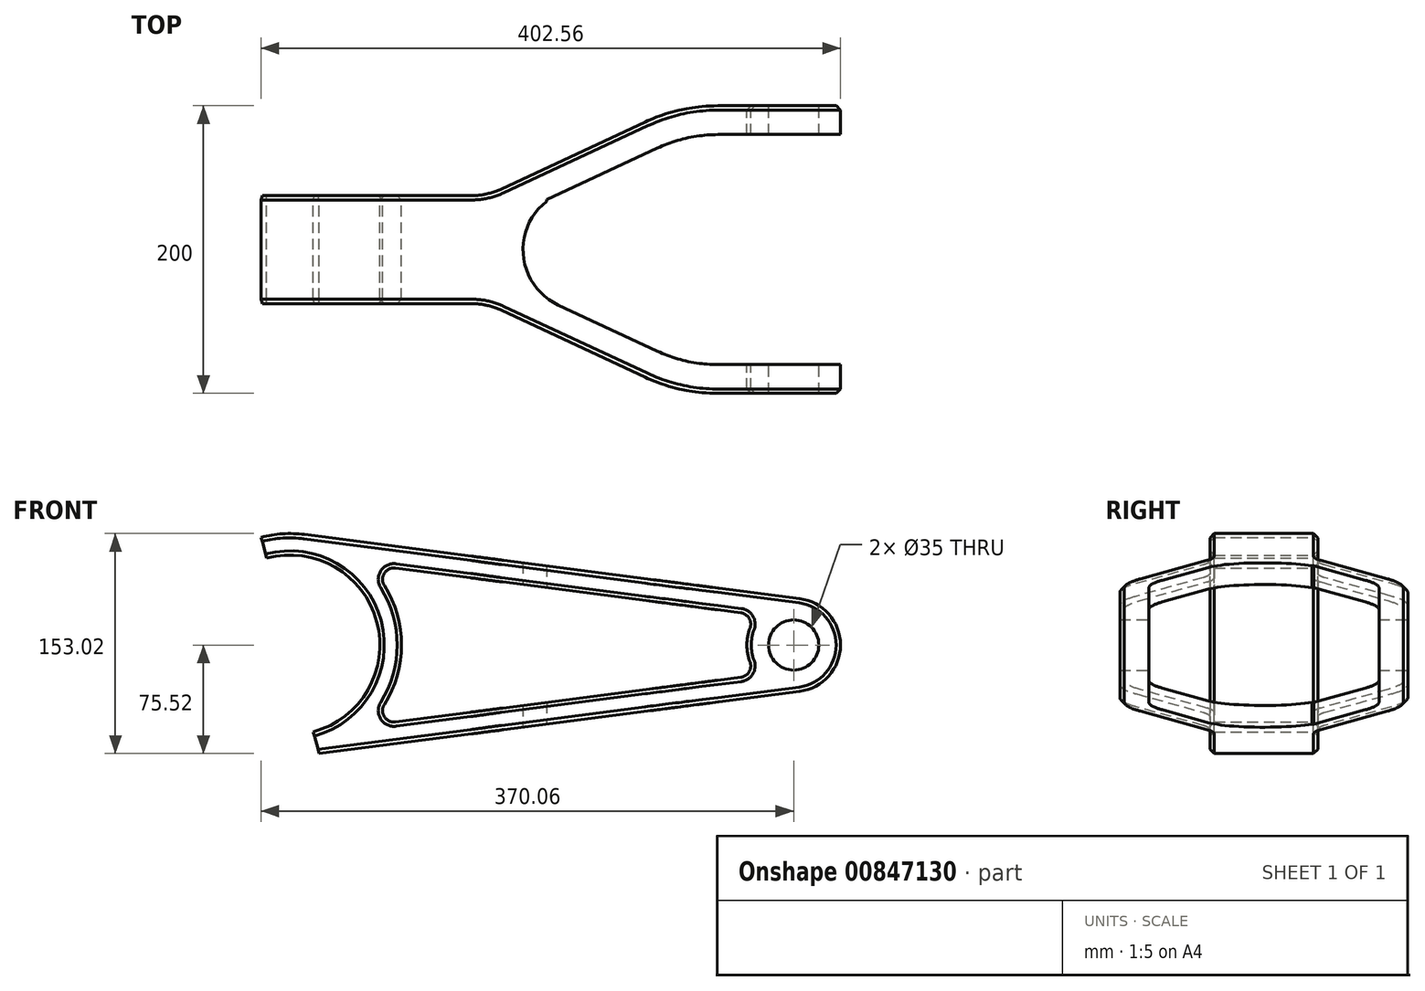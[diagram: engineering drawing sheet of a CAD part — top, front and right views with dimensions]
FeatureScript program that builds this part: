
annotation { "Feature Type Name" : "Feature", "Feature Type Description" : "" }
export const myFeature = defineFeature(function(context is Context, id is Id, definition is map)
    precondition{}
    {
        {
            var Q0;
            Q0=qCreatedBy(makeId("Top.planeOp"),FACE);
            var sketch = newSketch(context, id + "F0", { "sketchPlane" : qUnion([Q0])});
            skLineSegment(sketch, "E0", {"start": v(-175, 0) * mm, "end": v(53.2, 0) * mm, "construction": true});
            skLineSegment(sketch, "E1.bottom", {"start": v(207.5, 100) * mm, "end": v(122.5, 100) * mm});
            skLineSegment(sketch, "E1.top", {"start": v(207.5, -100) * mm, "end": v(-175, -100) * mm});
            skLineSegment(sketch, "E1.left", {"start": v(175, 100) * mm, "end": v(175, -100) * mm});
            skLineSegment(sketch, "E1.right", {"start": v(-175, 100) * mm, "end": v(-175, -100) * mm});
            skPoint(sketch, "E1.middle", {"position": v(0, 0) * mm});
            skLineSegment(sketch, "E2.0", {"start": v(207.5, 80) * mm, "end": v(122.5, 80) * mm});
            skLineSegment(sketch, "E3.0", {"start": v(122.5, 100) * mm, "end": v(122.5, -100) * mm, "construction": true});
            skLineSegment(sketch, "E4", {"start": v(80.24, 70.63) * mm, "end": v(11.37, 38.52) * mm});
            skArc(sketch, "E5", {"start": v(-13.17, 0) * mm, "mid": v(65.18, -22.84) * mm, "end": v(11.37, 38.52) * mm, "construction": true});
            skArc(sketch, "E6", {"start": v(11.37, 38.52) * mm, "mid": v(-6.51, 22.84) * mm, "end": v(-13.17, 0) * mm});
            skArc(sketch, "E7", {"start": v(80.24, 70.63) * mm, "mid": v(43.99, 41.93) * mm, "end": v(24.52, 0) * mm, "construction": true});
            skArc(sketch, "E8", {"start": v(24.52, 0) * mm, "mid": v(120.49, -119.98) * mm, "end": v(221.2, -3.96) * mm, "construction": true});
            skArc(sketch, "E9", {"start": v(122.5, 80) * mm, "mid": v(100.86, 77.63) * mm, "end": v(80.24, 70.63) * mm});
            skLineSegment(sketch, "E10", {"start": v(122.5, 80) * mm, "end": v(-175, 80) * mm});
            skArc(sketch, "E11", {"start": v(221.2, -3.96) * mm, "mid": v(187.3, 56.17) * mm, "end": v(122.5, 80) * mm, "construction": true});
            skLineSegment(sketch, "E12", {"start": v(11.37, 38.52) * mm, "end": v(-71.23, 0) * mm});
            skArc(sketch, "E13", {"start": v(122.5, 100) * mm, "mid": v(96.53, 97.16) * mm, "end": v(71.79, 88.76) * mm});
            skLineSegment(sketch, "E14.0", {"start": v(71.79, 88.76) * mm, "end": v(-118.55, 0) * mm});
            skPoint(sketch, "E15.orphan", {"position": v(-42.97, 0) * mm});
            skLineSegment(sketch, "E16", {"start": v(-175, 37.5) * mm, "end": v(-38.14, 37.5) * mm});
            skLineSegment(sketch, "E17.MirrorCS", {"start": v(-175, -37.5) * mm, "end": v(-38.14, -37.5) * mm});
            skLineSegment(sketch, "E18.MirrorCS", {"start": v(71.79, -88.76) * mm, "end": v(-118.55, 0) * mm});
            skLineSegment(sketch, "E19.MirrorCS", {"start": v(80.24, -70.63) * mm, "end": v(11.37, -38.52) * mm});
            skArc(sketch, "E20.MirrorCS", {"start": v(122.5, -80) * mm, "mid": v(100.86, -77.63) * mm, "end": v(80.24, -70.63) * mm});
            skLineSegment(sketch, "E21.MirrorCS", {"start": v(207.5, -80) * mm, "end": v(122.5, -80) * mm});
            skArc(sketch, "E22.MirrorCS", {"start": v(11.37, -38.52) * mm, "mid": v(-6.51, -22.84) * mm, "end": v(-13.17, 0) * mm});
            skLineSegment(sketch, "E23.0", {"start": v(207.5, 100) * mm, "end": v(207.5, -100) * mm});
            skPoint(sketch, "E24.orphan", {"position": v(175, 80) * mm});
            skPoint(sketch, "E25.orphan", {"position": v(175, -80) * mm});
            skArc(sketch, "E26", {"start": v(122.5, -100) * mm, "mid": v(96.53, -97.16) * mm, "end": v(71.79, -88.76) * mm});
            skArc(sketch, "E27", {"start": v(20.12, -42.6) * mm, "mid": v(19.73, -41.95) * mm, "end": v(19.34, -41.3) * mm});
            skLineSegment(sketch, "E28", {"start": v(122.5, 100) * mm, "end": v(-175, 100) * mm});
            skArc(sketch, "E29.trimOffspring", {"start": v(3.27, 33.57) * mm, "mid": v(3.34, 34.19) * mm, "end": v(3.42, 34.8) * mm});
            skArc(sketch, "E30.trimOffspring", {"start": v(20.12, 42.6) * mm, "mid": v(19.73, 41.95) * mm, "end": v(19.34, 41.3) * mm});
            skLineSegment(sketch, "E31.0", {"start": v(-205, 100) * mm, "end": v(-205, -100) * mm});
            skLineSegment(sketch, "E32", {"start": v(-175, -100) * mm, "end": v(-205, -100) * mm});
            skLineSegment(sketch, "E33", {"start": v(-175, 100) * mm, "end": v(-205, 100) * mm});
            skLineSegment(sketch, "E34", {"start": v(-175, 37.5) * mm, "end": v(-205, 37.5) * mm});
            skLineSegment(sketch, "E35", {"start": v(-175, -37.5) * mm, "end": v(-205, -37.5) * mm});
            skSolve(sketch);
        }
        {
            var Q0;
            {var subQ0=sQuery(id+"F0.wireOp",EDGE,"E34");Q0=makeQuery(id+"F0.imprint","IMPRINT",FACE,{"disambiguationData":[TD([[makeQuery(id+"F0.imprint","IMPRINT",EDGE,{"derivedFrom":subQ0}),1.0]])]});}
            var Q1;
            {var subQ1=sQuery(id+"F0.wireOp",EDGE,"E16");Q1=makeQuery(id+"F0.imprint","IMPRINT",FACE,{"disambiguationData":[TD([[makeQuery(id+"F0.imprint","IMPRINT",EDGE,{"derivedFrom":subQ1}),-1.0]])]});}
            var Q2;
            {var subQ9=sQuery(id+"F0.wireOp",EDGE,"E9");Q2=makeQuery(id+"F0.imprint","IMPRINT",FACE,{"disambiguationData":[TD([[makeQuery(id+"F0.imprint","IMPRINT",EDGE,{"derivedFrom":subQ9}),-1.0]])]});}
            var Q3;
            {var subQ9=sQuery(id+"F0.wireOp",EDGE,"E13");Q3=makeQuery(id+"F0.imprint","IMPRINT",FACE,{"disambiguationData":[TD([[makeQuery(id+"F0.imprint","IMPRINT",EDGE,{"derivedFrom":subQ9}),1.0]])]});}
            var Q4;
            {var subQ0=sQuery(id+"F0.wireOp",EDGE,"E23.0");var subQ1=sQuery(id+"F0.wireOp",EDGE,"E1.bottom");var subQ2=makeQuery(id+"F0.imprint","INTERSECT",VERTEX,{"derivedFrom":[subQ1,subQ0]});Q4=makeQuery(id+"F0.imprint","IMPRINT",FACE,{"disambiguationData":[TD([[makeQuery(id+"F0.imprint","IMPRINT",EDGE,{"disambiguationData":[TD([[subQ2,-1.0]])],"derivedFrom":subQ1}),1.0]])]});}
            var Q5;
            {var subQ0=sQuery(id+"F0.wireOp",EDGE,"E23.0");var subQ1=sQuery(id+"F0.wireOp",EDGE,"E1.top");var subQ2=makeQuery(id+"F0.imprint","INTERSECT",VERTEX,{"derivedFrom":[subQ1,subQ0]});Q5=makeQuery(id+"F0.imprint","IMPRINT",FACE,{"disambiguationData":[TD([[makeQuery(id+"F0.imprint","IMPRINT",EDGE,{"disambiguationData":[TD([[subQ2,-1.0]])],"derivedFrom":subQ1}),-1.0]])]});}
            var Q6;
            {var subQ3=sQuery(id+"F0.wireOp",EDGE,"E29.trimOffspring");Q6=makeQuery(id+"F0.imprint","IMPRINT",FACE,{"disambiguationData":[TD([[makeQuery(id+"F0.imprint","IMPRINT",EDGE,{"derivedFrom":subQ3}),-1.0]])]});}
            extrude(context, id + "F1", {"entities" : qUnion([Q0, Q1, Q2, Q3, Q4, Q5, Q6]), "endBound" : BoundingType.SYMMETRIC, "depth" : (77.5 * 2) * mm, "offsetDistance" : 25 * mm});
        }
        {
            var Q0;
            Q0=makeQuery(id+"F1.opExtrude","SWEPT_EDGE",EDGE,{"disambiguationData":[OSD([sQuery(id+"F0.wireOp",EDGE,"E14.0"),sQuery(id+"F0.wireOp",EDGE,"E16")])]});
            var Q1;
            Q1=makeQuery(id+"F1.opExtrude","SWEPT_EDGE",EDGE,{"disambiguationData":[OSD([sQuery(id+"F0.wireOp",EDGE,"E17.MirrorCS"),sQuery(id+"F0.wireOp",EDGE,"E18.MirrorCS")])]});
            fillet(context, id + "F2", {"entities" : qUnion([Q0, Q1]), "radius" : 50 * mm, "tangentPropagation" : true, "allowEdgeOverflow" : false});
        }
        {
            var Q0;
            Q0=qCreatedBy(makeId("Front.planeOp"),FACE);
            var sketch = newSketch(context, id + "F3", { "sketchPlane" : qUnion([Q0])});
            skPoint(sketch, "E36.0", {"position": v(175, 0) * mm});
            skLineSegment(sketch, "E37", {"start": v(175, 0) * mm, "end": v(175, 46.76) * mm, "construction": true});
            skCircle(sketch, "E38", {"center": v(175, 0) * mm, "radius": 17.5 * mm});
            skCircle(sketch, "E39", {"center": v(175, 0) * mm, "radius": 32.5 * mm});
            skPoint(sketch, "E40.0", {"position": v(-175, 0) * mm});
            skCircle(sketch, "E41", {"center": v(-175, 0) * mm, "radius": 62.5 * mm});
            skCircle(sketch, "E42", {"center": v(-175, 0) * mm, "radius": 77.5 * mm});
            skLineSegment(sketch, "E43", {"start": v(-165.04, 76.86) * mm, "end": v(179.18, 32.23) * mm});
            skLineSegment(sketch, "E44", {"start": v(-166.96, 61.98) * mm, "end": v(177.25, 17.35) * mm});
            skLineSegment(sketch, "E45.MirrorCS", {"start": v(-166.96, -61.98) * mm, "end": v(177.25, -17.35) * mm});
            skLineSegment(sketch, "E46.MirrorCS", {"start": v(-165.04, -76.86) * mm, "end": v(179.18, -32.23) * mm});
            skLineSegment(sketch, "E47", {"start": v(-212.33, 139.32) * mm, "end": v(-137.35, -140.53) * mm});
            skSolve(sketch);
        }
        {
            var Q0;
            {var subQ0=sQuery(id+"F3.wireOp",EDGE,"E43");Q0=makeQuery(id+"F3.imprint","IMPRINT",FACE,{"disambiguationData":[TD([[makeQuery(id+"F3.imprint","IMPRINT",EDGE,{"derivedFrom":subQ0}),-1.0]])]});}
            var Q1;
            {var subQ5=sQuery(id+"F3.wireOp",EDGE,"E44");var subQ7=sQuery(id+"F3.wireOp",EDGE,"E41");var subQ8=makeQuery(id+"F3.imprint","INTERSECT",VERTEX,{"derivedFrom":[subQ7,subQ5]});Q1=makeQuery(id+"F3.imprint","IMPRINT",FACE,{"disambiguationData":[TD([[makeQuery(id+"F3.imprint","IMPRINT",EDGE,{"disambiguationData":[TD([[subQ8,-1.0]])],"derivedFrom":subQ7}),-1.0]])]});}
            var Q2;
            {var subQ5=sQuery(id+"F3.wireOp",EDGE,"E44");var subQ6=sQuery(id+"F3.wireOp",EDGE,"E38");var subQ7=makeQuery(id+"F3.imprint","INTERSECT",VERTEX,{"derivedFrom":[subQ6,subQ5]});Q2=makeQuery(id+"F3.imprint","IMPRINT",FACE,{"disambiguationData":[TD([[makeQuery(id+"F3.imprint","IMPRINT",EDGE,{"disambiguationData":[TD([[subQ7,1.0]])],"derivedFrom":subQ6}),-1.0]])]});}
            var Q3;
            {var subQ0=sQuery(id+"F3.wireOp",EDGE,"E44");var subQ1=sQuery(id+"F3.wireOp",EDGE,"E41");var subQ2=makeQuery(id+"F3.imprint","INTERSECT",VERTEX,{"derivedFrom":[subQ1,subQ0]});Q3=makeQuery(id+"F3.imprint","IMPRINT",FACE,{"disambiguationData":[TD([[makeQuery(id+"F3.imprint","IMPRINT",EDGE,{"disambiguationData":[TD([[subQ2,1.0]])],"derivedFrom":subQ1}),-1.0]])]});}
            var Q4;
            {var subQ0=sQuery(id+"F3.wireOp",EDGE,"E44");var subQ1=sQuery(id+"F3.wireOp",EDGE,"E38");var subQ2=makeQuery(id+"F3.imprint","INTERSECT",VERTEX,{"derivedFrom":[subQ1,subQ0]});Q4=makeQuery(id+"F3.imprint","IMPRINT",FACE,{"disambiguationData":[TD([[makeQuery(id+"F3.imprint","IMPRINT",EDGE,{"disambiguationData":[TD([[subQ2,-1.0]])],"derivedFrom":subQ1}),-1.0]])]});}
            var Q5;
            {var subQ0=sQuery(id+"F3.wireOp",EDGE,"E47");var subQ1=sQuery(id+"F3.wireOp",EDGE,"E42");var subQ2=makeQuery(id+"F3.imprint","INTERSECT",VERTEX,{"disambiguationData":[OD(1.0)],"derivedFrom":[subQ1,subQ0]});Q5=makeQuery(id+"F3.imprint","IMPRINT",FACE,{"disambiguationData":[TD([[makeQuery(id+"F3.imprint","IMPRINT",EDGE,{"disambiguationData":[TD([[subQ2,-1.0]])],"derivedFrom":subQ1}),1.0]])]});}
            var Q6;
            {var subQ0=sQuery(id+"F3.wireOp",EDGE,"E46.MirrorCS");var subQ1=sQuery(id+"F3.wireOp",EDGE,"E39");var subQ2=makeQuery(id+"F3.imprint","INTERSECT",VERTEX,{"derivedFrom":[subQ1,subQ0]});Q6=makeQuery(id+"F3.imprint","IMPRINT",FACE,{"disambiguationData":[TD([[makeQuery(id+"F3.imprint","IMPRINT",EDGE,{"disambiguationData":[TD([[subQ2,1.0]])],"derivedFrom":subQ1}),-1.0]])]});}
            extrude(context, id + "F4", {"entities" : qUnion([Q0, Q1, Q2, Q3, Q4, Q5, Q6]), "endBound" : BoundingType.SYMMETRIC, "depth" : (100 * 2) * mm, "offsetDistance" : 25 * mm});
        }
        {
            var Q0;
            Q0=makeQuery(id+"F1.opExtrude","SWEPT_BODY",BODY,{"disambiguationData":[OSD([sQuery(id+"F0.wireOp",EDGE,"E1.bottom"),sQuery(id+"F0.wireOp",EDGE,"E1.top"),sQuery(id+"F0.wireOp",EDGE,"E1.right"),sQuery(id+"F0.wireOp",EDGE,"E2.0"),sQuery(id+"F0.wireOp",EDGE,"E4"),sQuery(id+"F0.wireOp",EDGE,"E6"),sQuery(id+"F0.wireOp",EDGE,"E9"),sQuery(id+"F0.wireOp",EDGE,"E12"),sQuery(id+"F0.wireOp",EDGE,"E13"),sQuery(id+"F0.wireOp",EDGE,"E14.0"),sQuery(id+"F0.wireOp",EDGE,"E16"),sQuery(id+"F0.wireOp",EDGE,"E17.MirrorCS"),sQuery(id+"F0.wireOp",EDGE,"E18.MirrorCS"),sQuery(id+"F0.wireOp",EDGE,"6e295972-1526-48e5-89e6-a9144c75bb0b0.MirrorC"),sQuery(id+"F0.wireOp",EDGE,"E19.MirrorCS"),sQuery(id+"F0.wireOp",EDGE,"E20.MirrorCS"),sQuery(id+"F0.wireOp",EDGE,"E21.MirrorCS"),sQuery(id+"F0.wireOp",EDGE,"E22.MirrorCS"),sQuery(id+"F0.wireOp",EDGE,"E23.0")])]});
            var Q1;
            Q1=makeQuery(id+"F4.opExtrude","SWEPT_BODY",BODY,{"disambiguationData":[OSD([sQuery(id+"F3.wireOp",EDGE,"E38"),sQuery(id+"F3.wireOp",EDGE,"E39"),sQuery(id+"F3.wireOp",EDGE,"E41"),sQuery(id+"F3.wireOp",EDGE,"E42"),sQuery(id+"F3.wireOp",EDGE,"E43"),sQuery(id+"F3.wireOp",EDGE,"E44"),sQuery(id+"F3.wireOp",EDGE,"E45.MirrorCS"),sQuery(id+"F3.wireOp",EDGE,"E46.MirrorCS"),sQuery(id+"F3.wireOp",EDGE,"E47")])]});
            booleanBodies(context, id + "F5", {"operationType" : BooleanOperationType.INTERSECTION, "tools" : qUnion([Q0, Q1])});
        }
        {
            var Q0;
            {var subQ0=sQuery(id+"F3.wireOp",EDGE,"E44");var subQ1=sQuery(id+"F3.wireOp",EDGE,"E39");Q0=makeQuery(id+"F5.opBoolean","SPLIT",EDGE,{"disambiguationData":[TD([makeQuery(id+"F1.opExtrude","SWEPT_FACE",FACE,{"disambiguationData":[OSD([sQuery(id+"F0.wireOp",EDGE,"E1.top")])]})])],"derivedFrom":makeQuery(id+"F4.opExtrude","SWEPT_EDGE",EDGE,{"disambiguationData":[OSD([subQ1,subQ0])]})});}
            var Q1;
            {var subQ0=sQuery(id+"F3.wireOp",EDGE,"E39");var subQ1=sQuery(id+"F3.wireOp",EDGE,"E45.MirrorCS");Q1=makeQuery(id+"F5.opBoolean","SPLIT",EDGE,{"disambiguationData":[TD([makeQuery(id+"F1.opExtrude","SWEPT_FACE",FACE,{"disambiguationData":[OSD([sQuery(id+"F0.wireOp",EDGE,"E1.top")])]})])],"derivedFrom":makeQuery(id+"F4.opExtrude","SWEPT_EDGE",EDGE,{"disambiguationData":[OSD([subQ0,subQ1])]})});}
            var Q2;
            {var subQ0=sQuery(id+"F3.wireOp",EDGE,"E45.MirrorCS");var subQ1=sQuery(id+"F3.wireOp",EDGE,"E39");Q2=makeQuery(id+"F5.opBoolean","SPLIT",EDGE,{"disambiguationData":[TD([makeQuery(id+"F1.opExtrude","SWEPT_FACE",FACE,{"disambiguationData":[OSD([sQuery(id+"F0.wireOp",EDGE,"E1.bottom")])]})])],"derivedFrom":makeQuery(id+"F4.opExtrude","SWEPT_EDGE",EDGE,{"disambiguationData":[OSD([subQ1,subQ0])]})});}
            var Q3;
            {var subQ0=sQuery(id+"F3.wireOp",EDGE,"E44");var subQ1=sQuery(id+"F3.wireOp",EDGE,"E39");Q3=makeQuery(id+"F5.opBoolean","SPLIT",EDGE,{"disambiguationData":[TD([makeQuery(id+"F1.opExtrude","SWEPT_FACE",FACE,{"disambiguationData":[OSD([sQuery(id+"F0.wireOp",EDGE,"E1.bottom")])]})])],"derivedFrom":makeQuery(id+"F4.opExtrude","SWEPT_EDGE",EDGE,{"disambiguationData":[OSD([subQ1,subQ0])]})});}
            fillet(context, id + "F6", {"entities" : qUnion([Q0, Q1, Q2, Q3]), "radius" : 8 * mm, "tangentPropagation" : true, "allowEdgeOverflow" : false});
        }
        {
            var Q0;
            Q0=makeQuery(id+"F4.opExtrude","SWEPT_EDGE",EDGE,{"disambiguationData":[OSD([sQuery(id+"F3.wireOp",EDGE,"E42"),sQuery(id+"F3.wireOp",EDGE,"E44")])]});
            var Q1;
            Q1=makeQuery(id+"F4.opExtrude","SWEPT_EDGE",EDGE,{"disambiguationData":[OSD([sQuery(id+"F3.wireOp",EDGE,"E42"),sQuery(id+"F3.wireOp",EDGE,"E45.MirrorCS")])]});
            fillet(context, id + "F7", {"entities" : qUnion([Q0, Q1]), "radius" : 8 * mm, "tangentPropagation" : true, "allowEdgeOverflow" : false});
        }
        {
            var Q0;
            Q0=makeQuery(id+"F5.opBoolean","INTERSECT",EDGE,{"derivedFrom":[makeQuery(id+"F1.opExtrude","SWEPT_FACE",FACE,{"disambiguationData":[OSD([sQuery(id+"F0.wireOp",EDGE,"E17.MirrorCS"),sQuery(id+"F0.wireOp",EDGE,"E35")])]}),makeQuery(id+"F4.opExtrude","SWEPT_FACE",FACE,{"disambiguationData":[OSD([sQuery(id+"F3.wireOp",EDGE,"E41")])]})]});
            var Q1;
            Q1=makeQuery(id+"F5.opBoolean","INTERSECT",EDGE,{"derivedFrom":[makeQuery(id+"F1.opExtrude","SWEPT_FACE",FACE,{"disambiguationData":[OSD([sQuery(id+"F0.wireOp",EDGE,"E17.MirrorCS"),sQuery(id+"F0.wireOp",EDGE,"E35")])]}),makeQuery(id+"F4.opExtrude","SWEPT_FACE",FACE,{"disambiguationData":[OSD([sQuery(id+"F3.wireOp",EDGE,"E43")])]})]});
            var Q2;
            Q2=makeQuery(id+"F4.opExtrude","CAP_EDGE",EDGE,{"disambiguationData":[OSD([sQuery(id+"F3.wireOp",EDGE,"E38")])],"isStart":false});
            var Q3;
            Q3=makeQuery(id+"F5.opBoolean","INTERSECT",EDGE,{"derivedFrom":[makeQuery(id+"F1.opExtrude","SWEPT_FACE",FACE,{"disambiguationData":[OSD([sQuery(id+"F0.wireOp",EDGE,"E17.MirrorCS"),sQuery(id+"F0.wireOp",EDGE,"E35")])]}),makeQuery(id+"F4.opExtrude","SWEPT_FACE",FACE,{"disambiguationData":[OSD([sQuery(id+"F3.wireOp",EDGE,"E45.MirrorCS")])]})]});
            var Q4;
            Q4=makeQuery(id+"F4.opExtrude","CAP_EDGE",EDGE,{"disambiguationData":[OSD([sQuery(id+"F3.wireOp",EDGE,"E38")])],"isStart":true});
            var Q5;
            Q5=makeQuery(id+"F5.opBoolean","INTERSECT",EDGE,{"derivedFrom":[makeQuery(id+"F1.opExtrude","SWEPT_FACE",FACE,{"disambiguationData":[OSD([sQuery(id+"F0.wireOp",EDGE,"E13")])]}),makeQuery(id+"F4.opExtrude","SWEPT_FACE",FACE,{"disambiguationData":[OSD([sQuery(id+"F3.wireOp",EDGE,"E45.MirrorCS")])]})]});
            var Q6;
            Q6=makeQuery(id+"F5.opBoolean","INTERSECT",EDGE,{"derivedFrom":[makeQuery(id+"F1.opExtrude","SWEPT_FACE",FACE,{"disambiguationData":[OSD([sQuery(id+"F0.wireOp",EDGE,"E14.0")])]}),makeQuery(id+"F4.opExtrude","SWEPT_FACE",FACE,{"disambiguationData":[OSD([sQuery(id+"F3.wireOp",EDGE,"E43")])]})]});
            var Q7;
            Q7=makeQuery(id+"F5.opBoolean","INTERSECT",EDGE,{"derivedFrom":[makeQuery(id+"F1.opExtrude","SWEPT_FACE",FACE,{"disambiguationData":[OSD([sQuery(id+"F0.wireOp",EDGE,"E16"),sQuery(id+"F0.wireOp",EDGE,"E34")])]}),makeQuery(id+"F4.opExtrude","SWEPT_FACE",FACE,{"disambiguationData":[OSD([sQuery(id+"F3.wireOp",EDGE,"E41")])]})]});
            chamfer(context, id + "F8", {"entities" : qUnion([Q0, Q1, Q2, Q3, Q4, Q5, Q6, Q7]), "chamferType" : ChamferType.OFFSET_ANGLE, "width" : 3 * mm, "oppositeDirection" : false, "angle" : 45 * degree, "tangentPropagation" : true});
        }
    });
